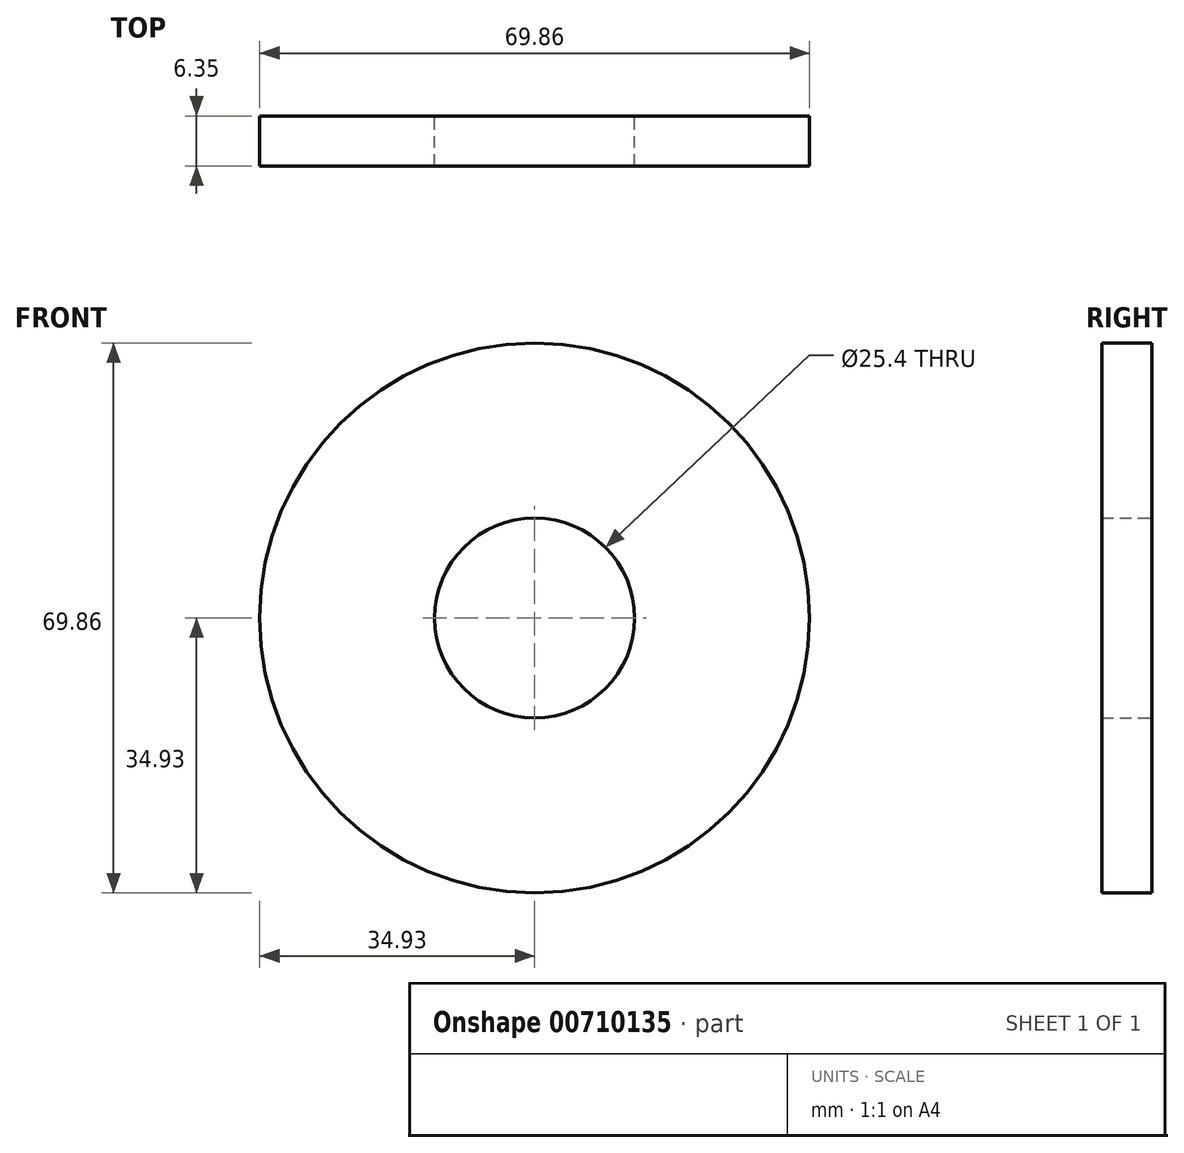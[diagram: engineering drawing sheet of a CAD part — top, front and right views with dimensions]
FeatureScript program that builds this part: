
annotation { "Feature Type Name" : "Feature", "Feature Type Description" : "" }
export const myFeature = defineFeature(function(context is Context, id is Id, definition is map)
    precondition{}
    {
        {
            var Q0;
            Q0=qCreatedBy(makeId("Front.planeOp"),FACE);
            var sketch = newSketch(context, id + "F0", { "sketchPlane" : qUnion([Q0])});
            skCircle(sketch, "E0", {"center": v(0, 0) * mm, "radius": 34.93 * mm});
            skCircle(sketch, "E1", {"center": v(0, 0) * mm, "radius": 12.7 * mm});
            skSolve(sketch);
        }
        {
            var Q0;
            Q0=makeQuery(id+"F0.imprint","IMPRINT",FACE,{"disambiguationData":[TD([[makeQuery(id+"F0.imprint","IMPRINT",EDGE,{"derivedFrom":sQuery(id+"F0.wireOp",EDGE,"E0")}),1.0]])]});
            extrude(context, id + "F1", {"entities" : qUnion([Q0]), "depth" : 6.35 * mm, "offsetDistance" : 25.4 * mm});
        }
    });
